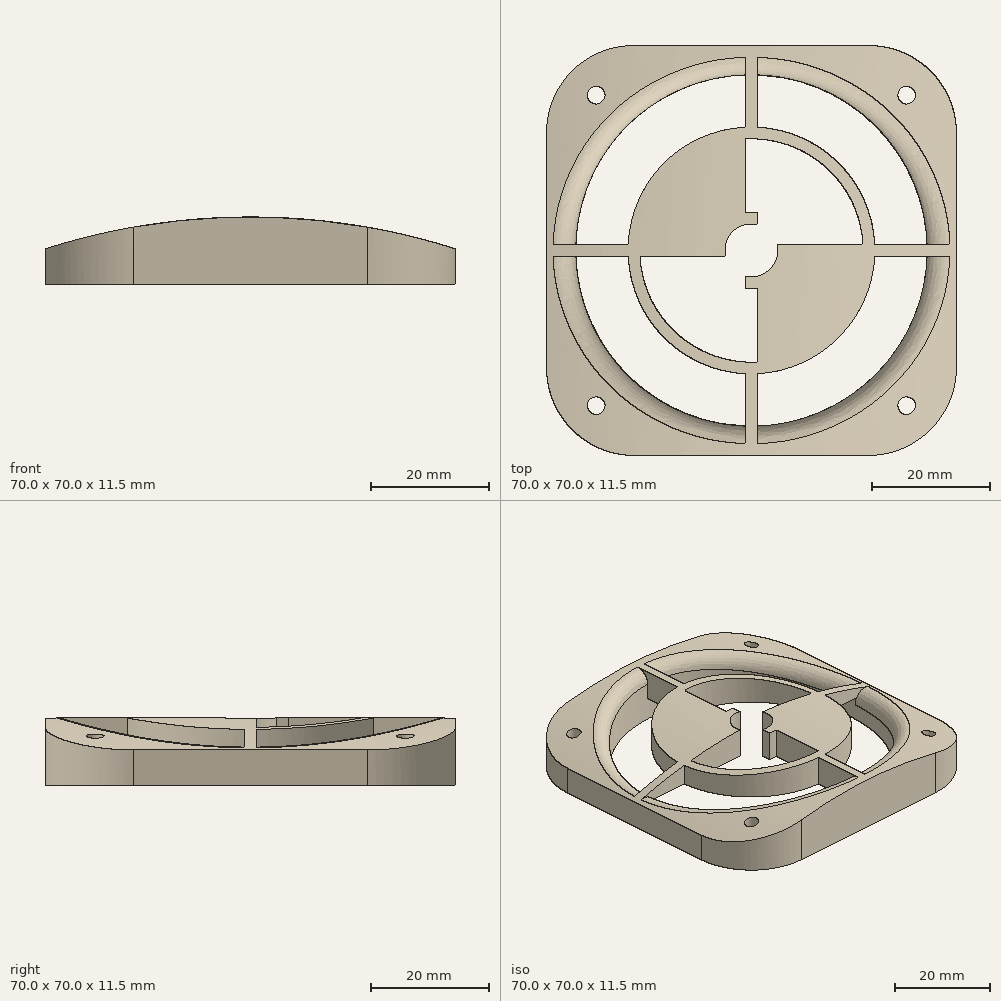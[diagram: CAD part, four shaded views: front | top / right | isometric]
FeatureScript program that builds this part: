
annotation { "Feature Type Name" : "Feature", "Feature Type Description" : "" }
export const myFeature = defineFeature(function(context is Context, id is Id, definition is map)
    precondition{}
    {
        {
            var Q0;
            Q0=qCreatedBy(makeId("Top.planeOp"),FACE);
            var sketch = newSketch(context, id + "F0", { "sketchPlane" : qUnion([Q0])});
            skLineSegment(sketch, "E0", {"start": v(0, 70.57) * mm, "end": v(0, -91.76) * mm, "construction": true});
            skLineSegment(sketch, "E1", {"start": v(-109.37, 0) * mm, "end": v(112.01, 0) * mm, "construction": true});
            skCircle(sketch, "E2", {"center": v(0, 0) * mm, "radius": 30 * mm});
            skLineSegment(sketch, "E3.bottom", {"start": v(35, 35) * mm, "end": v(-35, 35) * mm});
            skLineSegment(sketch, "E3.top", {"start": v(35, -35) * mm, "end": v(-35, -35) * mm});
            skLineSegment(sketch, "E3.left", {"start": v(35, 35) * mm, "end": v(35, -35) * mm});
            skLineSegment(sketch, "E3.right", {"start": v(-35, 35) * mm, "end": v(-35, -35) * mm});
            skLineSegment(sketch, "E4.bottom", {"start": v(26.5, 26.5) * mm, "end": v(-26.5, 26.5) * mm, "construction": true});
            skLineSegment(sketch, "E4.top", {"start": v(26.5, -26.5) * mm, "end": v(-26.5, -26.5) * mm, "construction": true});
            skLineSegment(sketch, "E4.left", {"start": v(26.5, 26.5) * mm, "end": v(26.5, -26.5) * mm, "construction": true});
            skLineSegment(sketch, "E4.right", {"start": v(-26.5, 26.5) * mm, "end": v(-26.5, -26.5) * mm, "construction": true});
            skCircle(sketch, "E5", {"center": v(26.5, 26.5) * mm, "radius": 1.5 * mm});
            skCircle(sketch, "E6.MirrorC", {"center": v(-26.5, 26.5) * mm, "radius": 1.5 * mm});
            skCircle(sketch, "E7.MirrorC", {"center": v(26.5, -26.5) * mm, "radius": 1.5 * mm});
            skCircle(sketch, "E8.MirrorC", {"center": v(-26.5, -26.5) * mm, "radius": 1.5 * mm});
            skCircle(sketch, "E9", {"center": v(0, 0) * mm, "radius": 6.52 * mm});
            skCircle(sketch, "E10.0", {"center": v(0, 0) * mm, "radius": 4.52 * mm});
            skCircle(sketch, "E11", {"center": v(0, 0) * mm, "radius": 19.07 * mm});
            skCircle(sketch, "E12.0", {"center": v(0, 0) * mm, "radius": 21.07 * mm});
            skLineSegment(sketch, "E13", {"start": v(-29.98, -1) * mm, "end": v(29.98, -1) * mm});
            skLineSegment(sketch, "E14.MirrorCS", {"start": v(-29.98, 1) * mm, "end": v(29.98, 1) * mm});
            skLineSegment(sketch, "E15", {"start": v(1, 29.98) * mm, "end": v(1, -29.98) * mm});
            skLineSegment(sketch, "E16.MirrorCS", {"start": v(-1, 29.98) * mm, "end": v(-1, -29.98) * mm});
            skSolve(sketch);
        }
        {
            var Q0;
            Q0 = qSketchRegion(id + "F0", true);
            var Q1;
            {var subQ0=sQuery(id+"F0.wireOp",EDGE,"E16.MirrorCS");var subQ1=sQuery(id+"F0.wireOp",EDGE,"E11");var subQ2=makeQuery(id+"F0.imprint","INTERSECT",VERTEX,{"disambiguationData":[OD(0.0)],"derivedFrom":[subQ1,subQ0]});Q1=makeQuery(id+"F0.imprint","IMPRINT",FACE,{"disambiguationData":[TD([[makeQuery(id+"F0.imprint","IMPRINT",EDGE,{"disambiguationData":[TD([[subQ2,-1.0]])],"derivedFrom":subQ1}),-1.0]])]});}
            var Q2;
            {var subQ0=sQuery(id+"F0.wireOp",EDGE,"E13");var subQ1=sQuery(id+"F0.wireOp",EDGE,"E2");var subQ2=makeQuery(id+"F0.imprint","INTERSECT",VERTEX,{"disambiguationData":[OD(0.0)],"derivedFrom":[subQ1,subQ0]});Q2=makeQuery(id+"F0.imprint","IMPRINT",FACE,{"disambiguationData":[TD([[makeQuery(id+"F0.imprint","IMPRINT",EDGE,{"disambiguationData":[TD([[subQ2,1.0]])],"derivedFrom":subQ1}),1.0]])]});}
            var Q3;
            {var subQ0=sQuery(id+"F0.wireOp",EDGE,"E13");var subQ1=sQuery(id+"F0.wireOp",EDGE,"E11");var subQ2=makeQuery(id+"F0.imprint","INTERSECT",VERTEX,{"disambiguationData":[OD(0.0)],"derivedFrom":[subQ1,subQ0]});Q3=makeQuery(id+"F0.imprint","IMPRINT",FACE,{"disambiguationData":[TD([[makeQuery(id+"F0.imprint","IMPRINT",EDGE,{"disambiguationData":[TD([[subQ2,-1.0]])],"derivedFrom":subQ1}),-1.0]])]});}
            var Q4;
            {var subQ0=sQuery(id+"F0.wireOp",EDGE,"E14.MirrorCS");var subQ1=sQuery(id+"F0.wireOp",EDGE,"E9");var subQ2=makeQuery(id+"F0.imprint","INTERSECT",VERTEX,{"disambiguationData":[OD(1.0)],"derivedFrom":[subQ1,subQ0]});Q4=makeQuery(id+"F0.imprint","IMPRINT",FACE,{"disambiguationData":[TD([[makeQuery(id+"F0.imprint","IMPRINT",EDGE,{"disambiguationData":[TD([[subQ2,-1.0]])],"derivedFrom":subQ1}),-1.0]])]});}
            var Q5;
            {var subQ0=sQuery(id+"F0.wireOp",EDGE,"E14.MirrorCS");var subQ1=sQuery(id+"F0.wireOp",EDGE,"E11");var subQ2=makeQuery(id+"F0.imprint","INTERSECT",VERTEX,{"disambiguationData":[OD(1.0)],"derivedFrom":[subQ1,subQ0]});Q5=makeQuery(id+"F0.imprint","IMPRINT",FACE,{"disambiguationData":[TD([[makeQuery(id+"F0.imprint","IMPRINT",EDGE,{"disambiguationData":[TD([[subQ2,-1.0]])],"derivedFrom":subQ1}),-1.0]])]});}
            var Q6;
            {var subQ0=sQuery(id+"F0.wireOp",EDGE,"E13");var subQ1=sQuery(id+"F0.wireOp",EDGE,"E9");var subQ2=makeQuery(id+"F0.imprint","INTERSECT",VERTEX,{"disambiguationData":[OD(0.0)],"derivedFrom":[subQ1,subQ0]});Q6=makeQuery(id+"F0.imprint","IMPRINT",FACE,{"disambiguationData":[TD([[makeQuery(id+"F0.imprint","IMPRINT",EDGE,{"disambiguationData":[TD([[subQ2,-1.0]])],"derivedFrom":subQ1}),1.0]])]});}
            var Q7;
            {var subQ0=sQuery(id+"F0.wireOp",EDGE,"E14.MirrorCS");var subQ1=sQuery(id+"F0.wireOp",EDGE,"E9");var subQ2=makeQuery(id+"F0.imprint","INTERSECT",VERTEX,{"disambiguationData":[OD(1.0)],"derivedFrom":[subQ1,subQ0]});Q7=makeQuery(id+"F0.imprint","IMPRINT",FACE,{"disambiguationData":[TD([[makeQuery(id+"F0.imprint","IMPRINT",EDGE,{"disambiguationData":[TD([[subQ2,-1.0]])],"derivedFrom":subQ1}),1.0]])]});}
            var Q8;
            {var subQ0=sQuery(id+"F0.wireOp",EDGE,"E16.MirrorCS");var subQ1=sQuery(id+"F0.wireOp",EDGE,"E9");var subQ2=makeQuery(id+"F0.imprint","INTERSECT",VERTEX,{"disambiguationData":[OD(0.0)],"derivedFrom":[subQ1,subQ0]});Q8=makeQuery(id+"F0.imprint","IMPRINT",FACE,{"disambiguationData":[TD([[makeQuery(id+"F0.imprint","IMPRINT",EDGE,{"disambiguationData":[TD([[subQ2,-1.0]])],"derivedFrom":subQ1}),1.0]])]});}
            var Q9;
            {var subQ0=sQuery(id+"F0.wireOp",EDGE,"E15");var subQ1=sQuery(id+"F0.wireOp",EDGE,"E9");var subQ2=makeQuery(id+"F0.imprint","INTERSECT",VERTEX,{"disambiguationData":[OD(0.0)],"derivedFrom":[subQ1,subQ0]});Q9=makeQuery(id+"F0.imprint","IMPRINT",FACE,{"disambiguationData":[TD([[makeQuery(id+"F0.imprint","IMPRINT",EDGE,{"disambiguationData":[TD([[subQ2,-1.0]])],"derivedFrom":subQ1}),1.0]])]});}
            var Q10;
            {var subQ0=sQuery(id+"F0.wireOp",EDGE,"E15");var subQ1=sQuery(id+"F0.wireOp",EDGE,"E9");var subQ2=makeQuery(id+"F0.imprint","INTERSECT",VERTEX,{"disambiguationData":[OD(0.0)],"derivedFrom":[subQ1,subQ0]});Q10=makeQuery(id+"F0.imprint","IMPRINT",FACE,{"disambiguationData":[TD([[makeQuery(id+"F0.imprint","IMPRINT",EDGE,{"disambiguationData":[TD([[subQ2,1.0]])],"derivedFrom":subQ1}),1.0]])]});}
            var Q11;
            {var subQ0=sQuery(id+"F0.wireOp",EDGE,"E14.MirrorCS");var subQ1=sQuery(id+"F0.wireOp",EDGE,"E9");var subQ2=makeQuery(id+"F0.imprint","INTERSECT",VERTEX,{"disambiguationData":[OD(0.0)],"derivedFrom":[subQ1,subQ0]});Q11=makeQuery(id+"F0.imprint","IMPRINT",FACE,{"disambiguationData":[TD([[makeQuery(id+"F0.imprint","IMPRINT",EDGE,{"disambiguationData":[TD([[subQ2,1.0]])],"derivedFrom":subQ1}),1.0]])]});}
            var Q12;
            {var subQ0=sQuery(id+"F0.wireOp",EDGE,"E15");var subQ1=sQuery(id+"F0.wireOp",EDGE,"E9");var subQ2=makeQuery(id+"F0.imprint","INTERSECT",VERTEX,{"disambiguationData":[OD(1.0)],"derivedFrom":[subQ1,subQ0]});Q12=makeQuery(id+"F0.imprint","IMPRINT",FACE,{"disambiguationData":[TD([[makeQuery(id+"F0.imprint","IMPRINT",EDGE,{"disambiguationData":[TD([[subQ2,-1.0]])],"derivedFrom":subQ1}),1.0]])]});}
            var Q13;
            {var subQ0=sQuery(id+"F0.wireOp",EDGE,"E16.MirrorCS");var subQ1=sQuery(id+"F0.wireOp",EDGE,"E11");var subQ2=makeQuery(id+"F0.imprint","INTERSECT",VERTEX,{"disambiguationData":[OD(1.0)],"derivedFrom":[subQ1,subQ0]});Q13=makeQuery(id+"F0.imprint","IMPRINT",FACE,{"disambiguationData":[TD([[makeQuery(id+"F0.imprint","IMPRINT",EDGE,{"disambiguationData":[TD([[subQ2,-1.0]])],"derivedFrom":subQ1}),-1.0]])]});}
            var Q14;
            {var subQ0=sQuery(id+"F0.wireOp",EDGE,"E15");var subQ1=sQuery(id+"F0.wireOp",EDGE,"E2");var subQ2=makeQuery(id+"F0.imprint","INTERSECT",VERTEX,{"disambiguationData":[OD(1.0)],"derivedFrom":[subQ1,subQ0]});Q14=makeQuery(id+"F0.imprint","IMPRINT",FACE,{"disambiguationData":[TD([[makeQuery(id+"F0.imprint","IMPRINT",EDGE,{"disambiguationData":[TD([[subQ2,1.0]])],"derivedFrom":subQ1}),1.0]])]});}
            var Q15;
            {var subQ0=sQuery(id+"F0.wireOp",EDGE,"E16.MirrorCS");var subQ1=sQuery(id+"F0.wireOp",EDGE,"E9");var subQ2=makeQuery(id+"F0.imprint","INTERSECT",VERTEX,{"disambiguationData":[OD(1.0)],"derivedFrom":[subQ1,subQ0]});Q15=makeQuery(id+"F0.imprint","IMPRINT",FACE,{"disambiguationData":[TD([[makeQuery(id+"F0.imprint","IMPRINT",EDGE,{"disambiguationData":[TD([[subQ2,-1.0]])],"derivedFrom":subQ1}),-1.0]])]});}
            var Q16;
            {var subQ0=sQuery(id+"F0.wireOp",EDGE,"E15");var subQ1=sQuery(id+"F0.wireOp",EDGE,"E11");var subQ2=makeQuery(id+"F0.imprint","INTERSECT",VERTEX,{"disambiguationData":[OD(1.0)],"derivedFrom":[subQ1,subQ0]});Q16=makeQuery(id+"F0.imprint","IMPRINT",FACE,{"disambiguationData":[TD([[makeQuery(id+"F0.imprint","IMPRINT",EDGE,{"disambiguationData":[TD([[subQ2,-1.0]])],"derivedFrom":subQ1}),-1.0]])]});}
            var Q17;
            {var subQ0=sQuery(id+"F0.wireOp",EDGE,"E14.MirrorCS");var subQ1=sQuery(id+"F0.wireOp",EDGE,"E11");var subQ2=makeQuery(id+"F0.imprint","INTERSECT",VERTEX,{"disambiguationData":[OD(0.0)],"derivedFrom":[subQ1,subQ0]});Q17=makeQuery(id+"F0.imprint","IMPRINT",FACE,{"disambiguationData":[TD([[makeQuery(id+"F0.imprint","IMPRINT",EDGE,{"disambiguationData":[TD([[subQ2,1.0]])],"derivedFrom":subQ1}),-1.0]])]});}
            var Q18;
            {var subQ0=sQuery(id+"F0.wireOp",EDGE,"E14.MirrorCS");var subQ1=sQuery(id+"F0.wireOp",EDGE,"E9");var subQ2=makeQuery(id+"F0.imprint","INTERSECT",VERTEX,{"disambiguationData":[OD(0.0)],"derivedFrom":[subQ1,subQ0]});Q18=makeQuery(id+"F0.imprint","IMPRINT",FACE,{"disambiguationData":[TD([[makeQuery(id+"F0.imprint","IMPRINT",EDGE,{"disambiguationData":[TD([[subQ2,1.0]])],"derivedFrom":subQ1}),-1.0]])]});}
            var Q19;
            {var subQ0=sQuery(id+"F0.wireOp",EDGE,"E15");var subQ1=sQuery(id+"F0.wireOp",EDGE,"E11");var subQ2=makeQuery(id+"F0.imprint","INTERSECT",VERTEX,{"disambiguationData":[OD(0.0)],"derivedFrom":[subQ1,subQ0]});Q19=makeQuery(id+"F0.imprint","IMPRINT",FACE,{"disambiguationData":[TD([[makeQuery(id+"F0.imprint","IMPRINT",EDGE,{"disambiguationData":[TD([[subQ2,1.0]])],"derivedFrom":subQ1}),-1.0]])]});}
            var Q20;
            {var subQ0=sQuery(id+"F0.wireOp",EDGE,"E15");var subQ1=sQuery(id+"F0.wireOp",EDGE,"E11");var subQ2=makeQuery(id+"F0.imprint","INTERSECT",VERTEX,{"disambiguationData":[OD(0.0)],"derivedFrom":[subQ1,subQ0]});Q20=makeQuery(id+"F0.imprint","IMPRINT",FACE,{"disambiguationData":[TD([[makeQuery(id+"F0.imprint","IMPRINT",EDGE,{"disambiguationData":[TD([[subQ2,-1.0]])],"derivedFrom":subQ1}),-1.0]])]});}
            var Q21;
            {var subQ0=sQuery(id+"F0.wireOp",EDGE,"E15");var subQ1=sQuery(id+"F0.wireOp",EDGE,"E2");var subQ2=makeQuery(id+"F0.imprint","INTERSECT",VERTEX,{"disambiguationData":[OD(0.0)],"derivedFrom":[subQ1,subQ0]});Q21=makeQuery(id+"F0.imprint","IMPRINT",FACE,{"disambiguationData":[TD([[makeQuery(id+"F0.imprint","IMPRINT",EDGE,{"disambiguationData":[TD([[subQ2,-1.0]])],"derivedFrom":subQ1}),1.0]])]});}
            var Q22;
            {var subQ0=sQuery(id+"F0.wireOp",EDGE,"E15");var subQ1=sQuery(id+"F0.wireOp",EDGE,"E9");var subQ2=makeQuery(id+"F0.imprint","INTERSECT",VERTEX,{"disambiguationData":[OD(0.0)],"derivedFrom":[subQ1,subQ0]});Q22=makeQuery(id+"F0.imprint","IMPRINT",FACE,{"disambiguationData":[TD([[makeQuery(id+"F0.imprint","IMPRINT",EDGE,{"disambiguationData":[TD([[subQ2,-1.0]])],"derivedFrom":subQ1}),-1.0]])]});}
            var Q23;
            {var subQ0=sQuery(id+"F0.wireOp",EDGE,"E16.MirrorCS");var subQ1=sQuery(id+"F0.wireOp",EDGE,"E9");var subQ2=makeQuery(id+"F0.imprint","INTERSECT",VERTEX,{"disambiguationData":[OD(1.0)],"derivedFrom":[subQ1,subQ0]});Q23=makeQuery(id+"F0.imprint","IMPRINT",FACE,{"disambiguationData":[TD([[makeQuery(id+"F0.imprint","IMPRINT",EDGE,{"disambiguationData":[TD([[subQ2,-1.0]])],"derivedFrom":subQ1}),1.0]])]});}
            var Q24;
            {var subQ0=sQuery(id+"F0.wireOp",EDGE,"E13");var subQ1=sQuery(id+"F0.wireOp",EDGE,"E2");var subQ2=makeQuery(id+"F0.imprint","INTERSECT",VERTEX,{"disambiguationData":[OD(1.0)],"derivedFrom":[subQ1,subQ0]});Q24=makeQuery(id+"F0.imprint","IMPRINT",FACE,{"disambiguationData":[TD([[makeQuery(id+"F0.imprint","IMPRINT",EDGE,{"disambiguationData":[TD([[subQ2,-1.0]])],"derivedFrom":subQ1}),1.0]])]});}
            extrude(context, id + "F1", {"entities" : qUnion([Q0, Q1, Q2, Q3, Q4, Q5, Q6, Q7, Q8, Q9, Q10, Q11, Q12, Q13, Q14, Q15, Q16, Q17, Q18, Q19, Q20, Q21, Q22, Q23, Q24]), "depth" : 25 * mm, "offsetDistance" : 25 * mm});
        }
        {
            var Q0;
            Q0=makeQuery(id+"F1.opExtrude","SWEPT_FACE",FACE,{"disambiguationData":[OSD([sQuery(id+"F0.wireOp",EDGE,"E3.top")])]});
            var sketch = newSketch(context, id + "F2", { "sketchPlane" : qUnion([Q0])});
            skPoint(sketch, "E17", {"position": v(-35, 6) * mm});
            skPoint(sketch, "E18", {"position": v(35, 6) * mm});
            skCircle(sketch, "E19", {"center": v(0, -103.54) * mm, "radius": 115 * mm});
            skPoint(sketch, "E19.third.point", {"position": v(3.15, -218.5) * mm});
            skSolve(sketch);
        }
        {
            var Q0;
            {var subQ1=sQuery(id+"F0.wireOp",EDGE,"E3.top");var subQ6=makeQuery(id+"F1.opExtrude","CAP_EDGE",EDGE,{"disambiguationData":[OSD([subQ1])],"isStart":false});Q0=makeQuery(id+"F2.imprint","IMPRINT",FACE,{"disambiguationData":[TD([[makeQuery(id+"F2.imprint","IMPRINT",EDGE,{"derivedFrom":subQ6}),1.0]])]});}
            extrude(context, id + "F3", {"entities" : qUnion([Q0]), "operationType" : NewBodyOperationType.REMOVE, "oppositeDirection" : true, "depth" : 76 * mm});
        }
        {
            var Q0;
            Q0=makeQuery(id+"F1.opExtrude","SWEPT_EDGE",EDGE,{"disambiguationData":[OSD([sQuery(id+"F0.wireOp",EDGE,"E3.bottom"),sQuery(id+"F0.wireOp",EDGE,"E3.left")])]});
            var Q1;
            Q1=makeQuery(id+"F1.opExtrude","SWEPT_EDGE",EDGE,{"disambiguationData":[OSD([sQuery(id+"F0.wireOp",EDGE,"E3.top"),sQuery(id+"F0.wireOp",EDGE,"E3.left")])]});
            var Q2;
            Q2=makeQuery(id+"F1.opExtrude","SWEPT_EDGE",EDGE,{"disambiguationData":[OSD([sQuery(id+"F0.wireOp",EDGE,"E3.bottom"),sQuery(id+"F0.wireOp",EDGE,"E3.right")])]});
            var Q3;
            Q3=makeQuery(id+"F1.opExtrude","SWEPT_EDGE",EDGE,{"disambiguationData":[OSD([sQuery(id+"F0.wireOp",EDGE,"E3.top"),sQuery(id+"F0.wireOp",EDGE,"E3.right")])]});
            fillet(context, id + "F4", {"entities" : qUnion([Q0, Q1, Q2, Q3]), "radius" : 15 * mm, "tangentPropagation" : true, "allowEdgeOverflow" : false});
        }
        {
            var Q0;
            Q0=makeQuery(id+"F3.boolean.opBoolean","INTERSECT",EDGE,{"derivedFrom":[makeQuery(id+"F1.opExtrude","SWEPT_FACE",FACE,{"disambiguationData":[OSD([sQuery(id+"F0.wireOp",EDGE,"E2")])]}),makeQuery(id+"F3.opExtrude","SWEPT_FACE",FACE,{"disambiguationData":[OSD([sQuery(id+"F2.wireOp",EDGE,"E19")])]})]});
            fillet(context, id + "F5", {"entities" : qUnion([Q0]), "radius" : 3 * mm, "tangentPropagation" : true, "allowEdgeOverflow" : false});
        }
        {
            var Q0;
            Q0=makeQuery(id+"F1.opExtrude","CAP_FACE",FACE,{"disambiguationData":[OSD([sQuery(id+"F0.wireOp",EDGE,"E2"),sQuery(id+"F0.wireOp",EDGE,"E3.bottom"),sQuery(id+"F0.wireOp",EDGE,"E3.top"),sQuery(id+"F0.wireOp",EDGE,"E3.left"),sQuery(id+"F0.wireOp",EDGE,"E3.right"),sQuery(id+"F0.wireOp",EDGE,"E5"),sQuery(id+"F0.wireOp",EDGE,"E6.MirrorC"),sQuery(id+"F0.wireOp",EDGE,"E7.MirrorC"),sQuery(id+"F0.wireOp",EDGE,"E8.MirrorC"),sQuery(id+"F0.wireOp",EDGE,"E9"),sQuery(id+"F0.wireOp",EDGE,"E10.0"),sQuery(id+"F0.wireOp",EDGE,"E11"),sQuery(id+"F0.wireOp",EDGE,"E12.0"),sQuery(id+"F0.wireOp",EDGE,"E13"),sQuery(id+"F0.wireOp",EDGE,"E14.MirrorCS"),sQuery(id+"F0.wireOp",EDGE,"E15"),sQuery(id+"F0.wireOp",EDGE,"E16.MirrorCS")])],"isStart":true});
            var sketch = newSketch(context, id + "F6", { "sketchPlane" : qUnion([Q0])});
            skCircle(sketch, "E20", {"center": v(0, 0) * mm, "radius": 30 * mm});
            skSolve(sketch);
        }
        {
            var Q0;
            Q0 = qSketchRegion(id + "F6", true);
            extrude(context, id + "F7", {"entities" : qUnion([Q0]), "operationType" : NewBodyOperationType.REMOVE, "oppositeDirection" : true, "depth" : 5 * mm});
        }
    });
